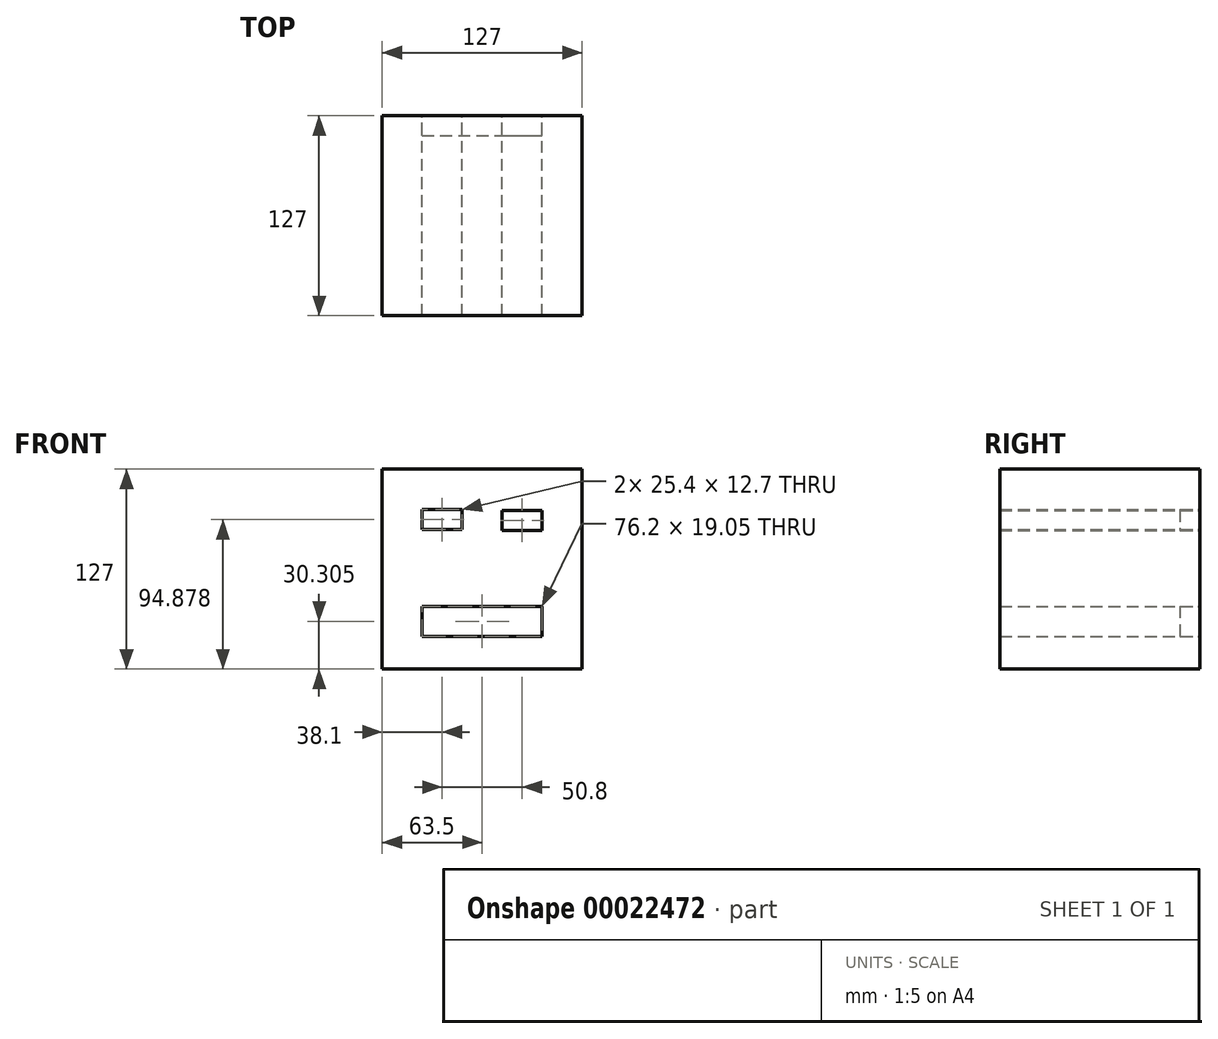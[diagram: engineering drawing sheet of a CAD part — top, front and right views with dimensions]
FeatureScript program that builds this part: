
annotation { "Feature Type Name" : "Feature", "Feature Type Description" : "" }
export const myFeature = defineFeature(function(context is Context, id is Id, definition is map)
    precondition{}
    {
        {
            var Q0;
            Q0=qCreatedBy(makeId("Front.planeOp"),FACE);
            var sketch = newSketch(context, id + "F0", { "sketchPlane" : qUnion([Q0])});
            skLineSegment(sketch, "E0.rect.bottom", {"start": v(-63.5, 63.5) * mm, "end": v(63.5, 63.5) * mm});
            skLineSegment(sketch, "E0.rect.top", {"start": v(-63.5, -63.5) * mm, "end": v(63.5, -63.5) * mm});
            skLineSegment(sketch, "E0.rect.left", {"start": v(-63.5, 63.5) * mm, "end": v(-63.5, -63.5) * mm});
            skLineSegment(sketch, "E0.rect.right", {"start": v(63.5, 63.5) * mm, "end": v(63.5, -63.5) * mm});
            skPoint(sketch, "E0.rect.middle", {"position": v(0, 0) * mm});
            skLineSegment(sketch, "E1.rect.bottom", {"start": v(-38.1, 37.73) * mm, "end": v(-12.7, 37.73) * mm});
            skLineSegment(sketch, "E1.rect.top", {"start": v(-38.1, 25.03) * mm, "end": v(-12.7, 25.03) * mm});
            skLineSegment(sketch, "E1.rect.left", {"start": v(-38.1, 37.73) * mm, "end": v(-38.1, 25.03) * mm});
            skLineSegment(sketch, "E1.rect.right", {"start": v(-12.7, 37.73) * mm, "end": v(-12.7, 25.03) * mm});
            skPoint(sketch, "E1.rect.middle", {"position": v(-25.4, 31.38) * mm});
            skLineSegment(sketch, "E2.rect.bottom", {"start": v(12.7, 37.32) * mm, "end": v(38.1, 37.32) * mm});
            skLineSegment(sketch, "E2.rect.top", {"start": v(12.7, 24.62) * mm, "end": v(38.1, 24.62) * mm});
            skLineSegment(sketch, "E2.rect.left", {"start": v(12.7, 37.32) * mm, "end": v(12.7, 24.62) * mm});
            skLineSegment(sketch, "E2.rect.right", {"start": v(38.1, 37.32) * mm, "end": v(38.1, 24.62) * mm});
            skPoint(sketch, "E2.rect.middle", {"position": v(25.4, 30.97) * mm});
            skLineSegment(sketch, "E3.rect.bottom", {"start": v(-38.1, -23.67) * mm, "end": v(38.1, -23.67) * mm});
            skLineSegment(sketch, "E3.rect.top", {"start": v(-38.1, -42.72) * mm, "end": v(38.1, -42.72) * mm});
            skLineSegment(sketch, "E3.rect.left", {"start": v(-38.1, -23.67) * mm, "end": v(-38.1, -42.72) * mm});
            skLineSegment(sketch, "E3.rect.right", {"start": v(38.1, -23.67) * mm, "end": v(38.1, -42.72) * mm});
            skPoint(sketch, "E3.rect.middle", {"position": v(0, -33.2) * mm});
            skSolve(sketch);
        }
        {
            var Q0;
            Q0=makeQuery(id+"F0.imprint","IMPRINT",FACE,{"disambiguationData":[TD([[makeQuery(id+"F0.imprint","IMPRINT",EDGE,{"derivedFrom":sQuery(id+"F0.wireOp",EDGE,"E1.rect.bottom")}),-1.0]])]});
            var Q1;
            Q1=makeQuery(id+"F0.imprint","IMPRINT",FACE,{"disambiguationData":[TD([[makeQuery(id+"F0.imprint","IMPRINT",EDGE,{"derivedFrom":sQuery(id+"F0.wireOp",EDGE,"E2.rect.bottom")}),-1.0]])]});
            var Q2;
            Q2=makeQuery(id+"F0.imprint","IMPRINT",FACE,{"disambiguationData":[TD([[makeQuery(id+"F0.imprint","IMPRINT",EDGE,{"derivedFrom":sQuery(id+"F0.wireOp",EDGE,"E3.rect.bottom")}),-1.0]])]});
            extrude(context, id + "F1", {"entities" : qUnion([Q0, Q1, Q2]), "depth" : 12.7 * mm});
        }
        {
            var Q0;
            Q0=makeQuery(id+"F0.imprint","IMPRINT",FACE,{"disambiguationData":[TD([[makeQuery(id+"F0.imprint","IMPRINT",EDGE,{"derivedFrom":sQuery(id+"F0.wireOp",EDGE,"E0.rect.bottom")}),-1.0]])]});
            extrude(context, id + "F2", {"entities" : qUnion([Q0]), "depth" : 127 * mm});
        }
    });
